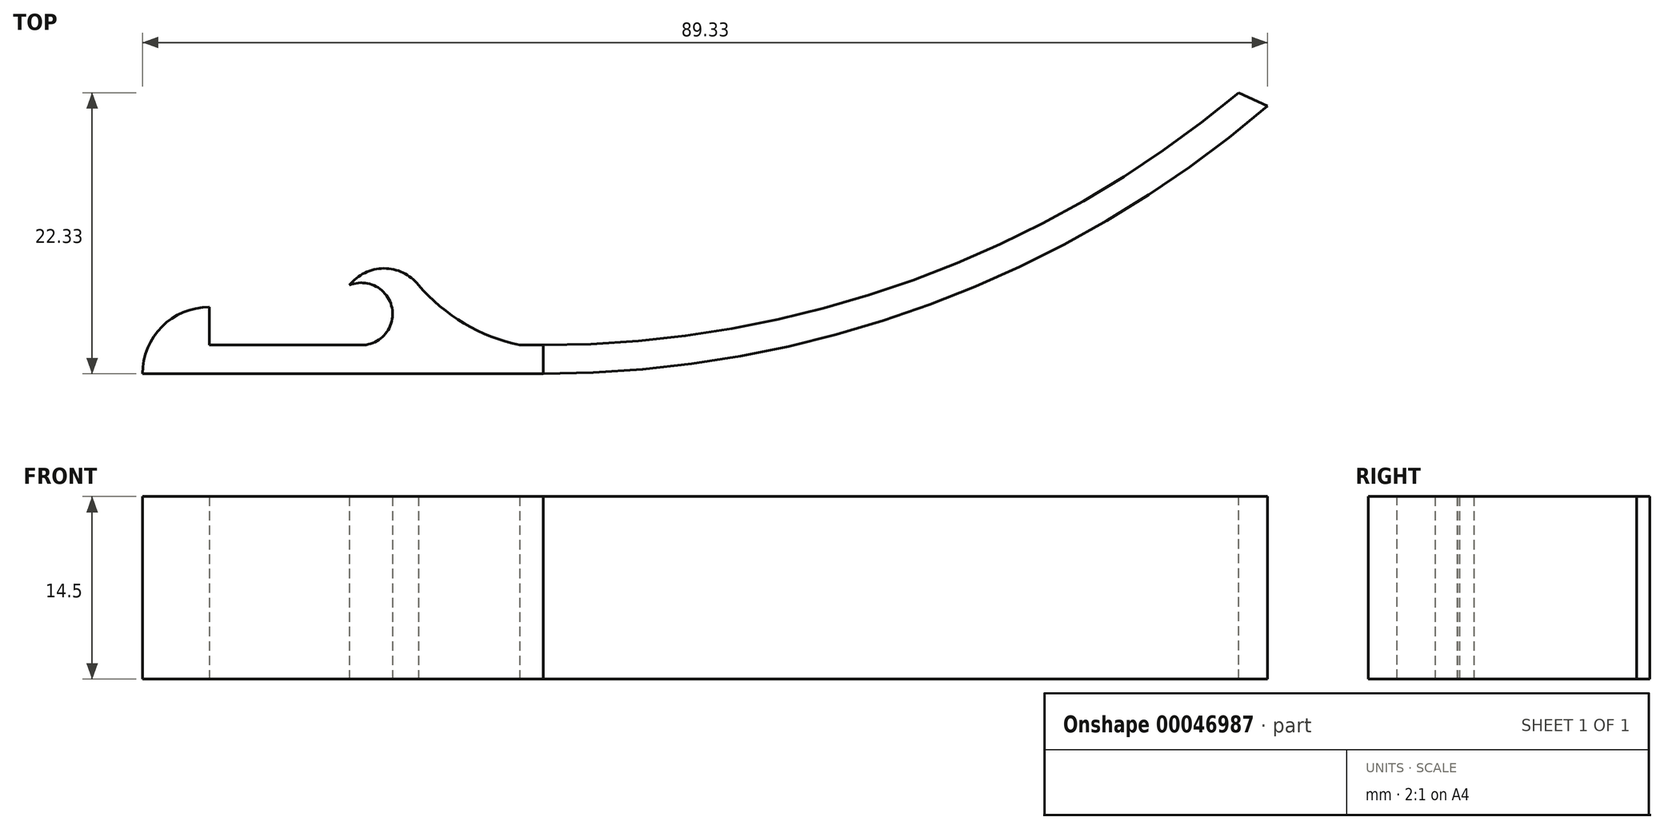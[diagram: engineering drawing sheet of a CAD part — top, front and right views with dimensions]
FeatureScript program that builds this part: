
annotation { "Feature Type Name" : "Feature", "Feature Type Description" : "" }
export const myFeature = defineFeature(function(context is Context, id is Id, definition is map)
    precondition{}
    {
        {
            var Q0;
            Q0=qCreatedBy(makeId("Top.planeOp"),FACE);
            var sketch = newSketch(context, id + "F0", { "sketchPlane" : qUnion([Q0])});
            skLineSegment(sketch, "E0", {"start": v(-11.96, 18.84) * mm, "end": v(-11.96, 15.82) * mm});
            skLineSegment(sketch, "E1", {"start": v(-11.96, 15.82) * mm, "end": v(2.6, 15.82) * mm});
            skLineSegment(sketch, "E2", {"start": v(2.6, 15.82) * mm, "end": v(2.6, 18.3) * mm, "construction": true});
            skPoint(sketch, "E3", {"position": v(0.12, 18.3) * mm});
            skArc(sketch, "E4", {"start": v(0.12, 15.82) * mm, "mid": v(2.55, 18.78) * mm, "end": v(-0.83, 20.58) * mm});
            skPoint(sketch, "E5", {"position": v(-11.96, 13.54) * mm});
            skArc(sketch, "E6", {"start": v(-11.96, 18.84) * mm, "mid": v(-15.71, 17.3) * mm, "end": v(-17.26, 13.54) * mm});
            skLineSegment(sketch, "E7", {"start": v(-17.26, 13.54) * mm, "end": v(-11.96, 13.54) * mm});
            skLineSegment(sketch, "E8", {"start": v(-11.96, 13.54) * mm, "end": v(2.66, 13.54) * mm});
            skArc(sketch, "E9", {"start": v(4.64, 20.6) * mm, "mid": v(1.9, 21.92) * mm, "end": v(-0.83, 20.58) * mm});
            skLineSegment(sketch, "E10", {"start": v(2.6, 15.82) * mm, "end": v(12.7, 15.82) * mm, "construction": true});
            skArc(sketch, "E11", {"start": v(4.64, 20.6) * mm, "mid": v(8.27, 17.55) * mm, "end": v(12.7, 15.82) * mm});
            skLineSegment(sketch, "E12", {"start": v(2.66, 13.54) * mm, "end": v(14.57, 13.54) * mm});
            skLineSegment(sketch, "E13", {"start": v(14.57, 15.82) * mm, "end": v(12.7, 15.82) * mm});
            skLineSegment(sketch, "E14", {"start": v(14.57, 13.54) * mm, "end": v(14.57, 15.82) * mm});
            skSolve(sketch);
        }
        {
            var Q0;
            {var subQ2=sQuery(id+"F0.wireOp",EDGE,"E0");Q0=makeQuery(id+"F0.imprint","IMPRINT",FACE,{"disambiguationData":[TD([[makeQuery(id+"F0.imprint","IMPRINT",EDGE,{"derivedFrom":subQ2}),-1.0]])]});}
            extrude(context, id + "F1", {"entities" : qUnion([Q0]), "depth" : 14.5 * mm});
        }
        {
            var Q0;
            Q0=makeQuery(id+"F1.opExtrude","CAP_FACE",FACE,{"disambiguationData":[OSD([sQuery(id+"F0.wireOp",EDGE,"E0"),sQuery(id+"F0.wireOp",EDGE,"E1"),sQuery(id+"F0.wireOp",EDGE,"E4"),sQuery(id+"F0.wireOp",EDGE,"E6"),sQuery(id+"F0.wireOp",EDGE,"E7"),sQuery(id+"F0.wireOp",EDGE,"E8"),sQuery(id+"F0.wireOp",EDGE,"E9"),sQuery(id+"F0.wireOp",EDGE,"E11"),sQuery(id+"F0.wireOp",EDGE,"E12"),sQuery(id+"F0.wireOp",EDGE,"E13"),sQuery(id+"F0.wireOp",EDGE,"E14")])],"isStart":false});
            var sketch = newSketch(context, id + "F2", { "sketchPlane" : qUnion([Q0])});
            skLineSegment(sketch, "E15", {"start": v(14.57, 15.82) * mm, "end": v(69.78, 15.82) * mm, "construction": true});
            skLineSegment(sketch, "E16", {"start": v(69.78, 15.82) * mm, "end": v(69.78, 35.87) * mm, "construction": true});
            skArc(sketch, "E17", {"start": v(14.57, 15.82) * mm, "mid": v(43.94, 20.99) * mm, "end": v(69.78, 35.87) * mm});
            skArc(sketch, "E18.0", {"start": v(14.57, 13.54) * mm, "mid": v(45.23, 19.03) * mm, "end": v(72.07, 34.82) * mm});
            skLineSegment(sketch, "E19", {"start": v(14.57, 13.54) * mm, "end": v(14.57, 15.82) * mm});
            skLineSegment(sketch, "E20", {"start": v(72.07, 34.82) * mm, "end": v(69.78, 35.87) * mm});
            skSolve(sketch);
        }
        {
            var Q0;
            {var subQ0=sQuery(id+"F2.wireOp",EDGE,"E17");Q0=makeQuery(id+"F2.imprint","IMPRINT",FACE,{"disambiguationData":[TD([[makeQuery(id+"F2.imprint","IMPRINT",EDGE,{"derivedFrom":subQ0}),-1.0]])]});}
            extrude(context, id + "F3", {"entities" : qUnion([Q0]), "oppositeDirection" : true, "depth" : 14.5 * mm});
        }
    });
